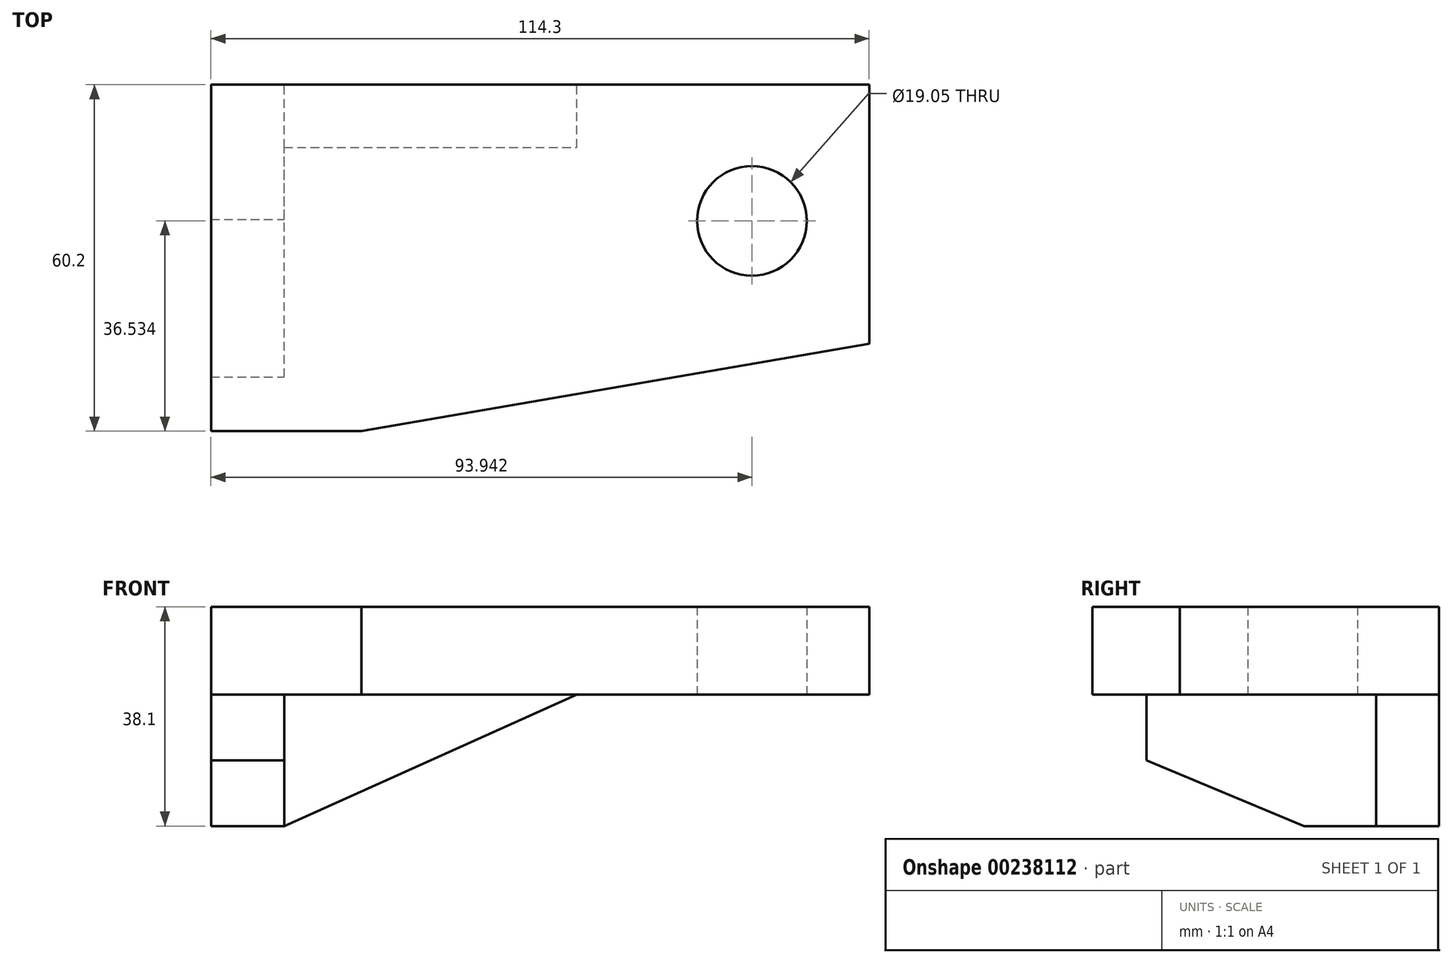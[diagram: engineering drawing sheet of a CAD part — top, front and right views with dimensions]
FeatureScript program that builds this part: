
annotation { "Feature Type Name" : "Feature", "Feature Type Description" : "" }
export const myFeature = defineFeature(function(context is Context, id is Id, definition is map)
    precondition{}
    {
        {
            var Q0;
            Q0=qCreatedBy(makeId("Front.planeOp"),FACE);
            var sketch = newSketch(context, id + "F0", { "sketchPlane" : qUnion([Q0])});
            skLineSegment(sketch, "E0.bottom", {"start": v(-53.22, 39.16) * mm, "end": v(61.08, 39.16) * mm});
            skLineSegment(sketch, "E0.top", {"start": v(-53.22, 23.92) * mm, "end": v(61.08, 23.92) * mm});
            skLineSegment(sketch, "E0.left", {"start": v(-53.22, 39.16) * mm, "end": v(-53.22, 23.92) * mm});
            skLineSegment(sketch, "E0.right", {"start": v(61.08, 39.16) * mm, "end": v(61.08, 23.92) * mm});
            skLineSegment(sketch, "E1.bottom", {"start": v(-53.22, 23.92) * mm, "end": v(10.28, 23.92) * mm});
            skLineSegment(sketch, "E1.top", {"start": v(-53.22, 1.06) * mm, "end": v(-40.52, 1.06) * mm});
            skLineSegment(sketch, "E1.left", {"start": v(-53.22, 23.92) * mm, "end": v(-53.22, 1.06) * mm});
            skLineSegment(sketch, "E2", {"start": v(10.28, 23.92) * mm, "end": v(-40.52, 1.06) * mm});
            skLineSegment(sketch, "E3", {"start": v(-13.24, 39.16) * mm, "end": v(-13.24, 23.92) * mm});
            skPoint(sketch, "E4", {"position": v(-13.24, 39.16) * mm});
            skLineSegment(sketch, "E5", {"start": v(-40.52, 1.06) * mm, "end": v(-40.52, 23.92) * mm});
            skSolve(sketch);
        }
        {
            var Q0;
            {var subQ3=sQuery(id+"F0.wireOp",EDGE,"E2");Q0=makeQuery(id+"F0.imprint","IMPRINT",FACE,{"disambiguationData":[TD([[makeQuery(id+"F0.imprint","IMPRINT",EDGE,{"derivedFrom":subQ3}),-1.0]])]});}
            extrude(context, id + "F1", {"entities" : qUnion([Q0]), "depth" : 10.92 * mm});
        }
        {
            var Q0;
            {var subQ3=sQuery(id+"F0.wireOp",EDGE,"E0.left");Q0=makeQuery(id+"F0.imprint","IMPRINT",FACE,{"disambiguationData":[TD([[makeQuery(id+"F0.imprint","IMPRINT",EDGE,{"derivedFrom":subQ3}),1.0]])]});}
            var Q1;
            {var subQ1=sQuery(id+"F0.wireOp",EDGE,"E0.top");Q1=makeQuery(id+"F0.imprint","IMPRINT",FACE,{"disambiguationData":[TD([[makeQuery(id+"F0.imprint","IMPRINT",EDGE,{"derivedFrom":subQ1}),1.0]])]});}
            extrude(context, id + "F2", {"entities" : qUnion([Q0, Q1]), "operationType" : NewBodyOperationType.ADD, "depth" : 60.2 * mm});
        }
        {
            var Q0;
            Q0=makeQuery(id+"F0.imprint","IMPRINT",FACE,{"disambiguationData":[TD([[makeQuery(id+"F0.imprint","IMPRINT",EDGE,{"derivedFrom":sQuery(id+"F0.wireOp",EDGE,"E1.top")}),1.0]])]});
            extrude(context, id + "F3", {"entities" : qUnion([Q0]), "operationType" : NewBodyOperationType.ADD, "depth" : 50.8 * mm});
        }
        {
            var Q0;
            Q0=makeQuery(id+"F3.opExtrude","SWEPT_FACE",FACE,{"disambiguationData":[OSD([sQuery(id+"F0.wireOp",EDGE,"E5")])]});
            var sketch = newSketch(context, id + "F4", { "sketchPlane" : qUnion([Q0])});
            skLineSegment(sketch, "E6", {"start": v(-50.8, 12.5) * mm, "end": v(-23.44, 1.06) * mm});
            skLineSegment(sketch, "E7", {"start": v(-23.44, 1.06) * mm, "end": v(-50.8, 1.06) * mm});
            skLineSegment(sketch, "E8", {"start": v(-50.8, 1.06) * mm, "end": v(-50.8, 12.5) * mm});
            skSolve(sketch);
        }
        {
            var Q0;
            Q0 = qSketchRegion(id + "F4", true);
            extrude(context, id + "F5", {"entities" : qUnion([Q0]), "operationType" : NewBodyOperationType.REMOVE, "oppositeDirection" : true, "depth" : 25.4 * mm});
        }
        {
            var Q0;
            Q0=makeQuery(id+"F2.opExtrude","SWEPT_FACE",FACE,{"disambiguationData":[OSD([sQuery(id+"F0.wireOp",EDGE,"E0.top"),sQuery(id+"F0.wireOp",EDGE,"E1.bottom")])]});
            var sketch = newSketch(context, id + "F6", { "sketchPlane" : qUnion([Q0])});
            skLineSegment(sketch, "E9", {"start": v(-27.1, 60.2) * mm, "end": v(61.08, 45.03) * mm});
            skLineSegment(sketch, "E10", {"start": v(61.08, 45.03) * mm, "end": v(61.08, 60.2) * mm});
            skLineSegment(sketch, "E11", {"start": v(61.08, 60.2) * mm, "end": v(-27.1, 60.2) * mm});
            skCircle(sketch, "E12", {"center": v(40.72, 23.67) * mm, "radius": 9.53 * mm});
            skSolve(sketch);
        }
        {
            var Q0;
            Q0 = qSketchRegion(id + "F6", true);
            extrude(context, id + "F7", {"entities" : qUnion([Q0]), "operationType" : NewBodyOperationType.REMOVE, "oppositeDirection" : true, "depth" : 25.4 * mm});
        }
        {
            var Q0;
            Q0 = qSketchRegion(id + "F6", true);
            extrude(context, id + "F8", {"entities" : qUnion([Q0]), "operationType" : NewBodyOperationType.REMOVE, "oppositeDirection" : true, "depth" : 25.4 * mm});
        }
    });
